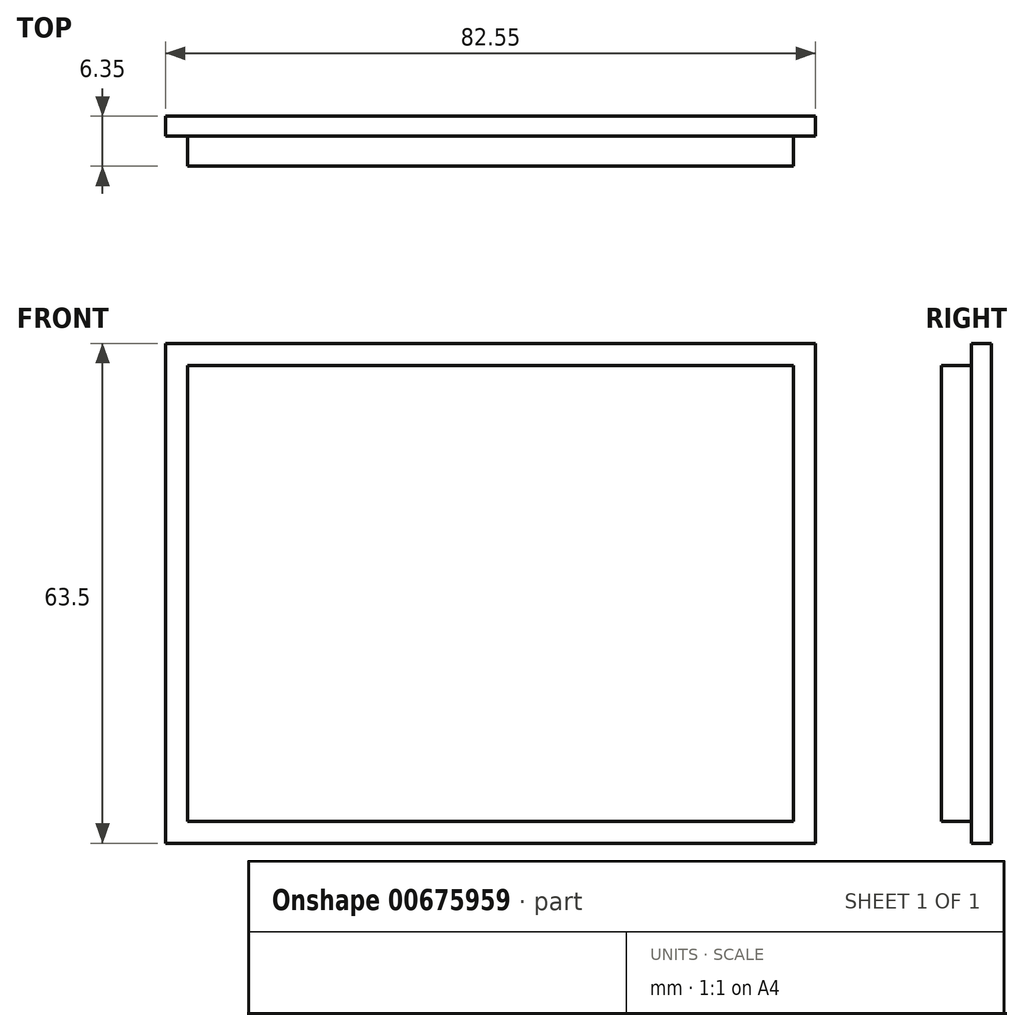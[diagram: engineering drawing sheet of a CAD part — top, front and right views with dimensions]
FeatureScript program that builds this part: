
annotation { "Feature Type Name" : "Feature", "Feature Type Description" : "" }
export const myFeature = defineFeature(function(context is Context, id is Id, definition is map)
    precondition{}
    {
        {
            var Q0;
            Q0=qCreatedBy(makeId("Front.planeOp"),FACE);
            var sketch = newSketch(context, id + "F0", { "sketchPlane" : qUnion([Q0])});
            skLineSegment(sketch, "E0.bottom", {"start": v(-36.96, 31.6) * mm, "end": v(45.6, 31.6) * mm});
            skLineSegment(sketch, "E0.top", {"start": v(-36.96, -31.9) * mm, "end": v(45.6, -31.9) * mm});
            skLineSegment(sketch, "E0.left", {"start": v(-36.96, 31.6) * mm, "end": v(-36.96, -31.9) * mm});
            skLineSegment(sketch, "E0.right", {"start": v(45.6, 31.6) * mm, "end": v(45.6, -31.9) * mm});
            skSolve(sketch);
        }
        {
            var Q0;
            Q0=makeQuery(id+"F0.imprint","IMPRINT",FACE,{"disambiguationData":[TD([[makeQuery(id+"F0.imprint","IMPRINT",EDGE,{"derivedFrom":sQuery(id+"F0.wireOp",EDGE,"E0.bottom")}),-1.0]])]});
            extrude(context, id + "F1", {"entities" : qUnion([Q0]), "depth" : 2.54 * mm, "offsetDistance" : 25.4 * mm});
        }
        {
            var Q0;
            Q0=makeQuery(id+"F1.opExtrude","CAP_FACE",FACE,{"disambiguationData":[OSD([sQuery(id+"F0.wireOp",EDGE,"E0.bottom"),sQuery(id+"F0.wireOp",EDGE,"E0.top"),sQuery(id+"F0.wireOp",EDGE,"E0.left"),sQuery(id+"F0.wireOp",EDGE,"E0.right")])],"isStart":false});
            var sketch = newSketch(context, id + "F2", { "sketchPlane" : qUnion([Q0])});
            skLineSegment(sketch, "E1.0", {"start": v(-34.16, 28.81) * mm, "end": v(-34.16, -29.1) * mm});
            skLineSegment(sketch, "E1.1", {"start": v(42.8, 28.81) * mm, "end": v(-34.16, 28.81) * mm});
            skLineSegment(sketch, "E1.2", {"start": v(42.8, -29.1) * mm, "end": v(42.8, 28.81) * mm});
            skLineSegment(sketch, "E1.3", {"start": v(-34.16, -29.1) * mm, "end": v(42.8, -29.1) * mm});
            skSolve(sketch);
        }
        {
            var Q0;
            Q0=makeQuery(id+"F2.imprint","IMPRINT",FACE,{"disambiguationData":[TD([[makeQuery(id+"F2.imprint","IMPRINT",EDGE,{"derivedFrom":sQuery(id+"F2.wireOp",EDGE,"E1.0")}),1.0]])]});
            extrude(context, id + "F3", {"entities" : qUnion([Q0]), "operationType" : NewBodyOperationType.ADD, "depth" : 3.8 * mm, "offsetDistance" : 25.4 * mm});
        }
    });
